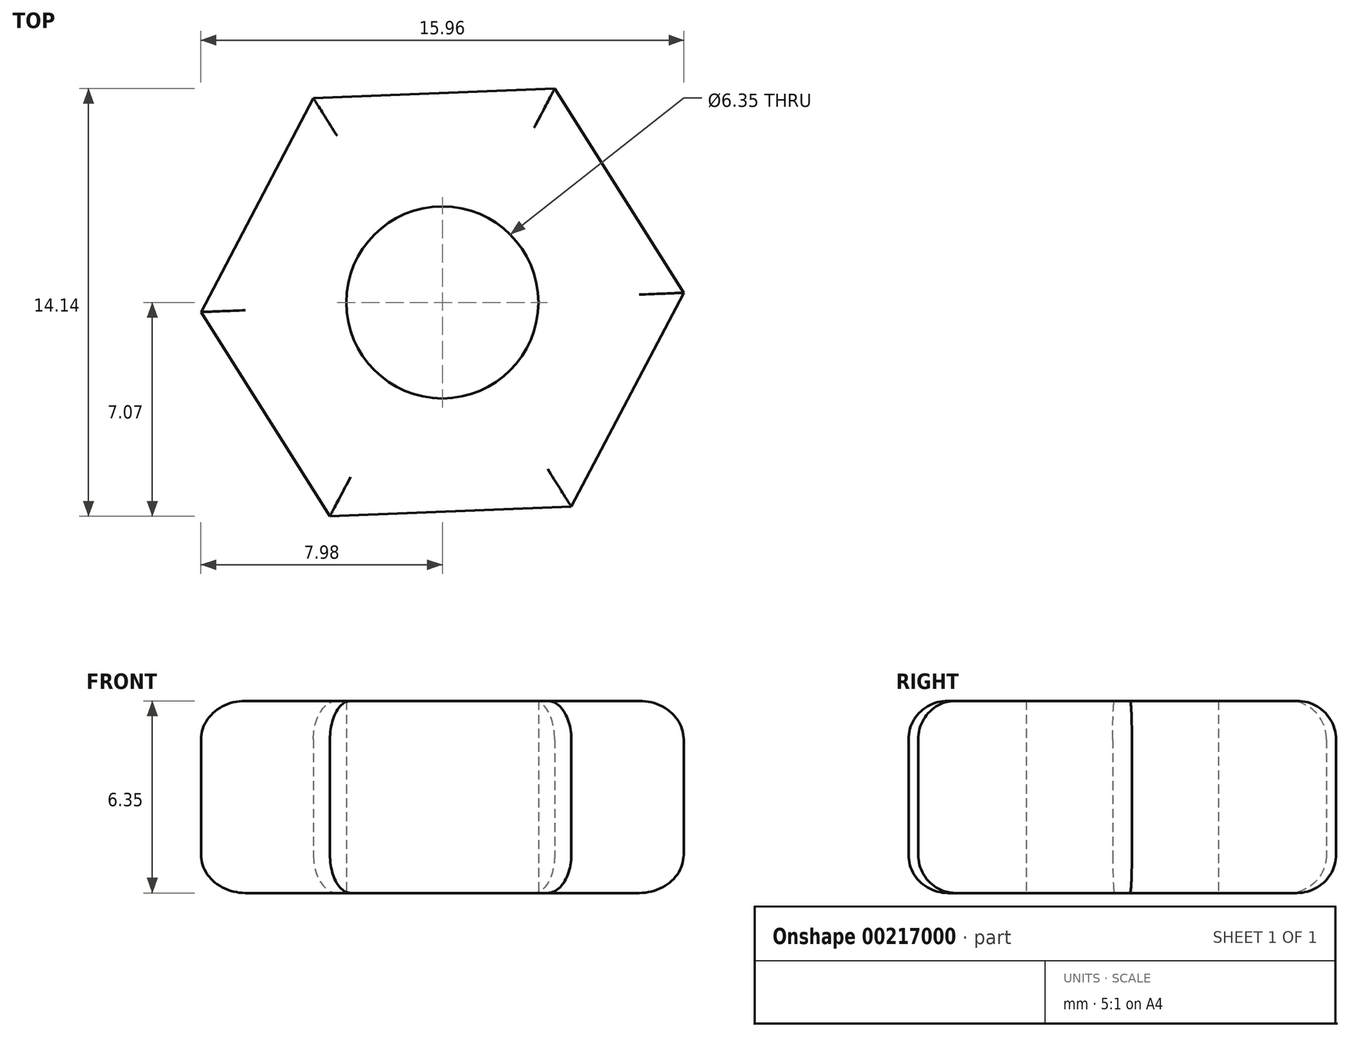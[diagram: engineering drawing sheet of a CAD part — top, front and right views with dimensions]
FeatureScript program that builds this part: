
annotation { "Feature Type Name" : "Feature", "Feature Type Description" : "" }
export const myFeature = defineFeature(function(context is Context, id is Id, definition is map)
    precondition{}
    {
        {
            var Q0;
            Q0=qCreatedBy(makeId("Top.planeOp"),FACE);
            var sketch = newSketch(context, id + "F0", { "sketchPlane" : qUnion([Q0])});
            skCircle(sketch, "E0", {"center": v(0, 0) * mm, "radius": 3.18 * mm});
            skCircle(sketch, "E1.cCircle", {"center": v(0, 0) * mm, "radius": 6.91 * mm, "construction": true});
            skLineSegment(sketch, "E1.0", {"start": v(7.98, 0.32) * mm, "end": v(4.26, -6.75) * mm});
            skLineSegment(sketch, "E1.1", {"start": v(4.26, -6.75) * mm, "end": v(-3.71, -7.07) * mm});
            skLineSegment(sketch, "E1.2", {"start": v(-3.71, -7.07) * mm, "end": v(-7.98, -0.32) * mm});
            skLineSegment(sketch, "E1.3", {"start": v(-7.98, -0.32) * mm, "end": v(-4.26, 6.75) * mm});
            skLineSegment(sketch, "E1.4", {"start": v(-4.26, 6.75) * mm, "end": v(3.71, 7.07) * mm});
            skLineSegment(sketch, "E1.5", {"start": v(3.71, 7.07) * mm, "end": v(7.98, 0.32) * mm});
            skPoint(sketch, "E1.0.midPoint", {"position": v(6.12, -3.22) * mm});
            skSolve(sketch);
        }
        {
            var Q0;
            Q0=makeQuery(id+"F0.imprint","IMPRINT",FACE,{"disambiguationData":[TD([[makeQuery(id+"F0.imprint","IMPRINT",EDGE,{"derivedFrom":sQuery(id+"F0.wireOp",EDGE,"E0")}),-1.0]])]});
            extrude(context, id + "F1", {"entities" : qUnion([Q0]), "depth" : 6.35 * mm});
        }
        {
            var Q0;
            Q0=makeQuery(id+"F1.opExtrude","CAP_EDGE",EDGE,{"disambiguationData":[OSD([sQuery(id+"F0.wireOp",EDGE,"E1.1")])],"isStart":false});
            var Q1;
            Q1=makeQuery(id+"F1.opExtrude","CAP_EDGE",EDGE,{"disambiguationData":[OSD([sQuery(id+"F0.wireOp",EDGE,"E1.0")])],"isStart":false});
            var Q2;
            Q2=makeQuery(id+"F1.opExtrude","CAP_EDGE",EDGE,{"disambiguationData":[OSD([sQuery(id+"F0.wireOp",EDGE,"E1.5")])],"isStart":false});
            var Q3;
            Q3=makeQuery(id+"F1.opExtrude","CAP_EDGE",EDGE,{"disambiguationData":[OSD([sQuery(id+"F0.wireOp",EDGE,"E1.4")])],"isStart":false});
            var Q4;
            Q4=makeQuery(id+"F1.opExtrude","CAP_EDGE",EDGE,{"disambiguationData":[OSD([sQuery(id+"F0.wireOp",EDGE,"E1.3")])],"isStart":false});
            var Q5;
            Q5=makeQuery(id+"F1.opExtrude","CAP_EDGE",EDGE,{"disambiguationData":[OSD([sQuery(id+"F0.wireOp",EDGE,"E1.2")])],"isStart":false});
            var Q6;
            Q6=makeQuery(id+"F1.opExtrude","CAP_EDGE",EDGE,{"disambiguationData":[OSD([sQuery(id+"F0.wireOp",EDGE,"E1.0")])],"isStart":true});
            var Q7;
            Q7=makeQuery(id+"F1.opExtrude","CAP_EDGE",EDGE,{"disambiguationData":[OSD([sQuery(id+"F0.wireOp",EDGE,"E1.1")])],"isStart":true});
            var Q8;
            Q8=makeQuery(id+"F1.opExtrude","CAP_EDGE",EDGE,{"disambiguationData":[OSD([sQuery(id+"F0.wireOp",EDGE,"E1.2")])],"isStart":true});
            var Q9;
            Q9=makeQuery(id+"F1.opExtrude","CAP_EDGE",EDGE,{"disambiguationData":[OSD([sQuery(id+"F0.wireOp",EDGE,"E1.3")])],"isStart":true});
            var Q10;
            Q10=makeQuery(id+"F1.opExtrude","CAP_EDGE",EDGE,{"disambiguationData":[OSD([sQuery(id+"F0.wireOp",EDGE,"E1.4")])],"isStart":true});
            var Q11;
            Q11=makeQuery(id+"F1.opExtrude","CAP_EDGE",EDGE,{"disambiguationData":[OSD([sQuery(id+"F0.wireOp",EDGE,"E1.5")])],"isStart":true});
            fillet(context, id + "F2", {"entities" : qUnion([Q0, Q1, Q2, Q3, Q4, Q5, Q6, Q7, Q8, Q9, Q10, Q11]), "radius" : 1.27 * mm, "tangentPropagation" : true, "allowEdgeOverflow" : false});
        }
    });
